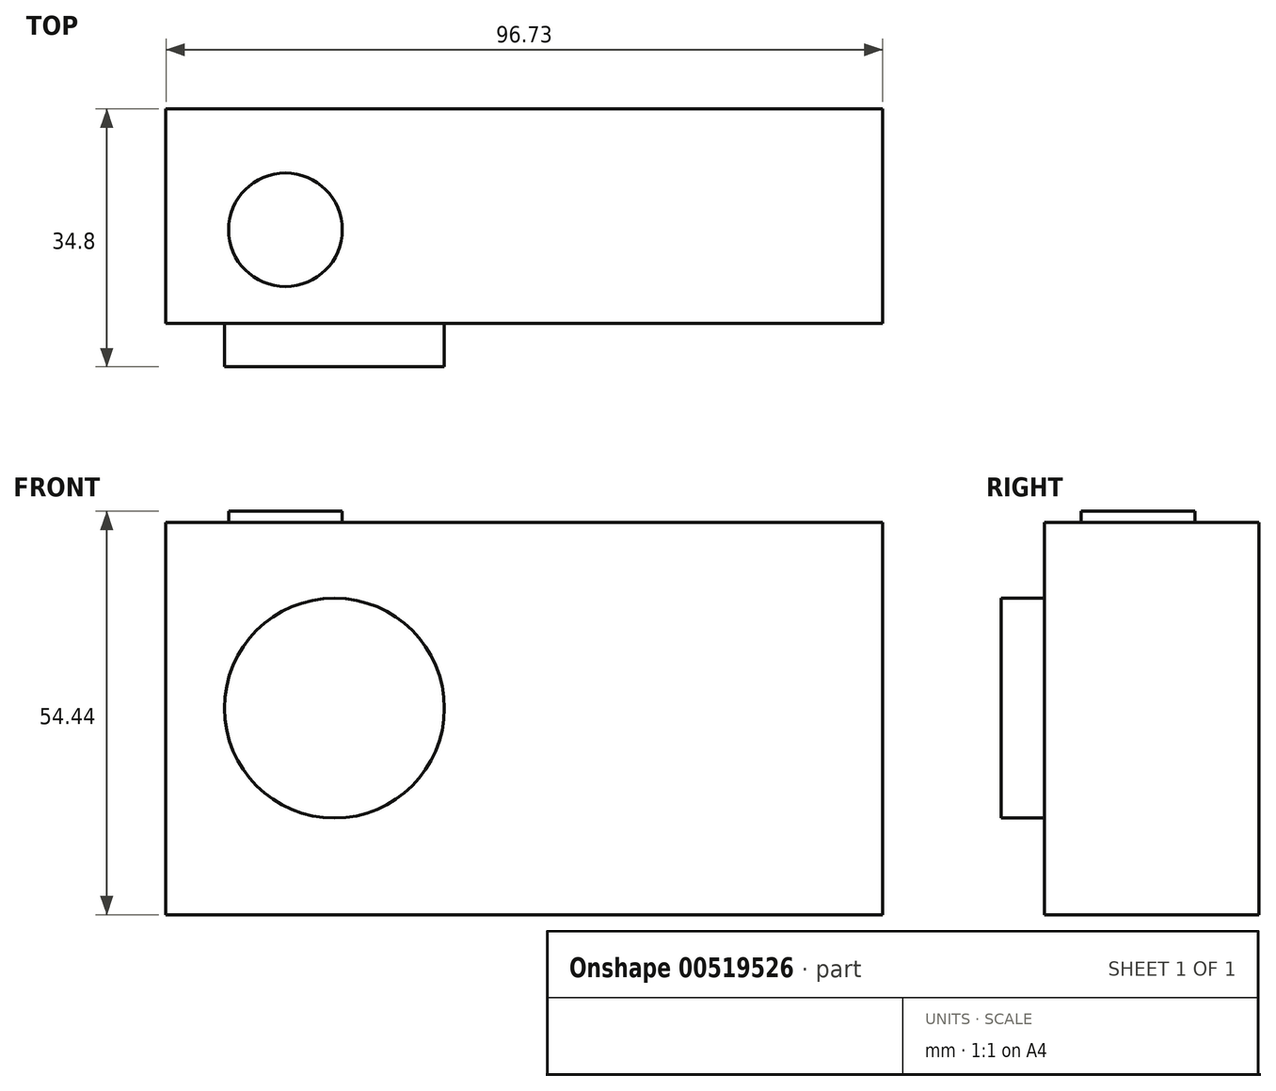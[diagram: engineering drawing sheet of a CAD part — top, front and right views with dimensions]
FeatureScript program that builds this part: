
annotation { "Feature Type Name" : "Feature", "Feature Type Description" : "" }
export const myFeature = defineFeature(function(context is Context, id is Id, definition is map)
    precondition{}
    {
        {
            var Q0;
            Q0=qCreatedBy(makeId("Front.planeOp"),FACE);
            var sketch = newSketch(context, id + "F0", { "sketchPlane" : qUnion([Q0])});
            skLineSegment(sketch, "E0.bottom", {"start": v(-96.73, 44.54) * mm, "end": v(0, 44.54) * mm});
            skLineSegment(sketch, "E0.top", {"start": v(-96.73, -8.37) * mm, "end": v(0, -8.37) * mm});
            skLineSegment(sketch, "E0.left", {"start": v(-96.73, 44.54) * mm, "end": v(-96.73, -8.37) * mm});
            skLineSegment(sketch, "E0.right", {"start": v(0, 44.54) * mm, "end": v(0, -8.37) * mm});
            skSolve(sketch);
        }
        {
            var Q0;
            Q0=makeQuery(id+"F0.imprint","IMPRINT",FACE,{"disambiguationData":[TD([[makeQuery(id+"F0.imprint","IMPRINT",EDGE,{"derivedFrom":sQuery(id+"F0.wireOp",EDGE,"E0.bottom")}),-1.0]])]});
            extrude(context, id + "F1", {"entities" : qUnion([Q0]), "depth" : 28.96 * mm, "offsetDistance" : 25.4 * mm});
        }
        {
            var Q0;
            Q0=makeQuery(id+"F1.opExtrude","CAP_FACE",FACE,{"disambiguationData":[OSD([sQuery(id+"F0.wireOp",EDGE,"E0.bottom"),sQuery(id+"F0.wireOp",EDGE,"E0.top"),sQuery(id+"F0.wireOp",EDGE,"E0.left"),sQuery(id+"F0.wireOp",EDGE,"E0.right")])],"isStart":false});
            var sketch = newSketch(context, id + "F2", { "sketchPlane" : qUnion([Q0])});
            skCircle(sketch, "E1", {"center": v(-74, 19.5) * mm, "radius": 14.84 * mm});
            skSolve(sketch);
        }
        {
            var Q0;
            Q0=makeQuery(id+"F2.imprint","IMPRINT",FACE,{"disambiguationData":[TD([[makeQuery(id+"F2.imprint","IMPRINT",EDGE,{"derivedFrom":sQuery(id+"F2.wireOp",EDGE,"E1")}),1.0]])]});
            extrude(context, id + "F3", {"entities" : qUnion([Q0]), "operationType" : NewBodyOperationType.ADD, "depth" : 5.84 * mm, "offsetDistance" : 25.4 * mm});
        }
        {
            var Q0;
            Q0=makeQuery(id+"F1.opExtrude","SWEPT_FACE",FACE,{"disambiguationData":[OSD([sQuery(id+"F0.wireOp",EDGE,"E0.bottom")])]});
            var sketch = newSketch(context, id + "F4", { "sketchPlane" : qUnion([Q0])});
            skCircle(sketch, "E2", {"center": v(-80.6, -16.3) * mm, "radius": 7.67 * mm});
            skSolve(sketch);
        }
        {
            var Q0;
            Q0=makeQuery(id+"F4.imprint","IMPRINT",FACE,{"disambiguationData":[TD([[makeQuery(id+"F4.imprint","IMPRINT",EDGE,{"derivedFrom":sQuery(id+"F4.wireOp",EDGE,"E2")}),1.0]])]});
            extrude(context, id + "F5", {"entities" : qUnion([Q0]), "operationType" : NewBodyOperationType.ADD, "depth" : 1.52 * mm, "offsetDistance" : 25.4 * mm});
        }
    });
